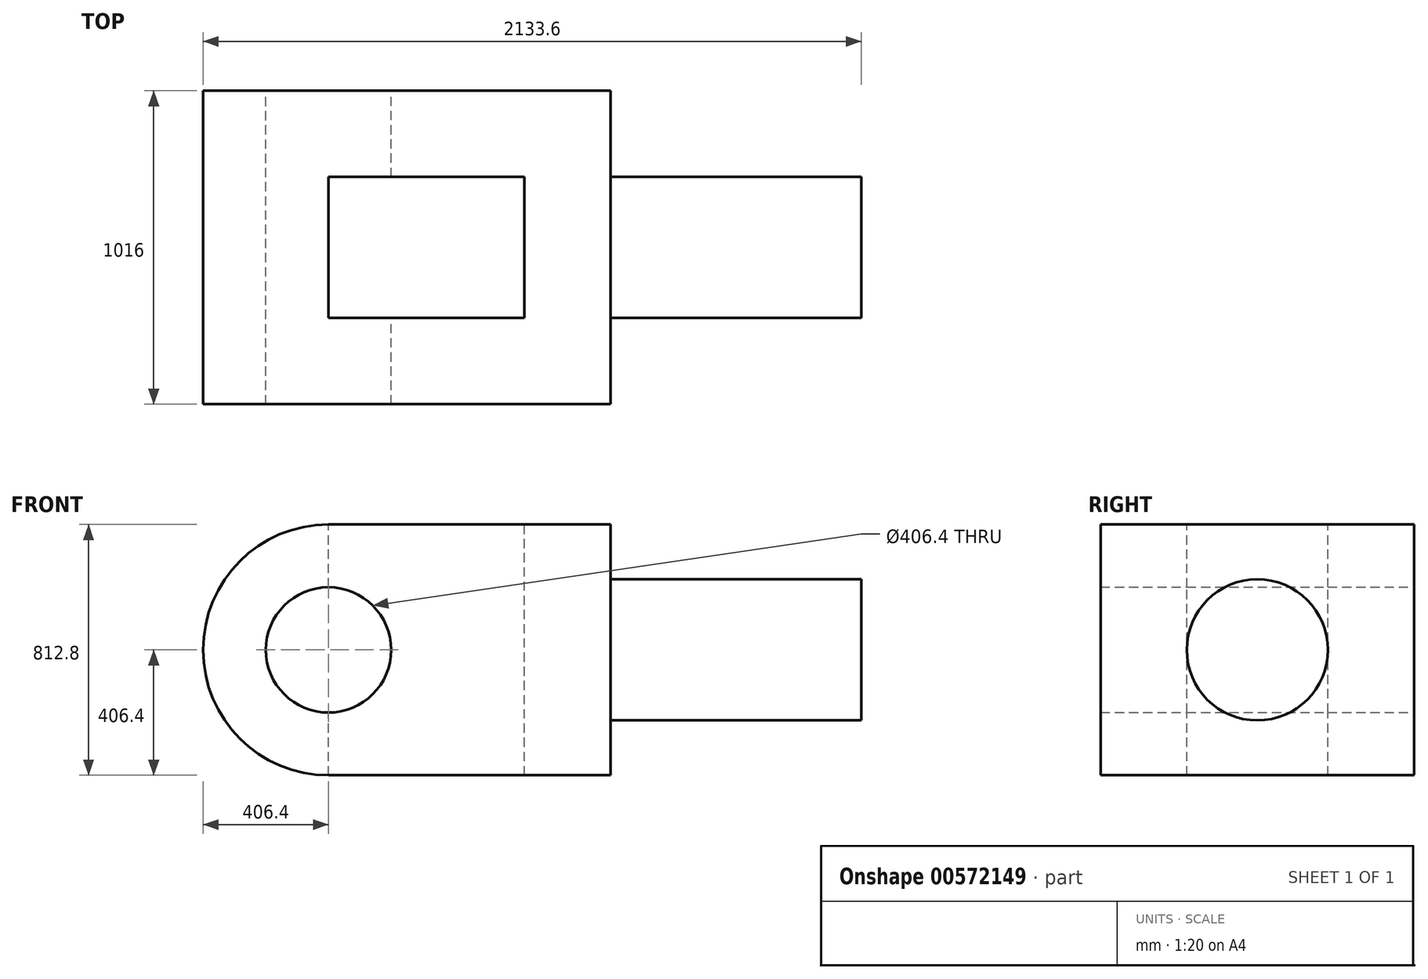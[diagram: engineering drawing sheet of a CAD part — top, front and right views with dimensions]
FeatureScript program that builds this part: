
annotation { "Feature Type Name" : "Feature", "Feature Type Description" : "" }
export const myFeature = defineFeature(function(context is Context, id is Id, definition is map)
    precondition{}
    {
        {
            var Q0;
            Q0=qCreatedBy(makeId("Front.planeOp"),FACE);
            var sketch = newSketch(context, id + "F0", { "sketchPlane" : qUnion([Q0])});
            skCircle(sketch, "E0", {"center": v(0, 0) * mm, "radius": 203.2 * mm});
            skCircle(sketch, "E1", {"center": v(0, 0) * mm, "radius": 406.4 * mm});
            skLineSegment(sketch, "E2", {"start": v(0, 406.4) * mm, "end": v(914.4, 406.4) * mm});
            skLineSegment(sketch, "E3", {"start": v(0, -406.4) * mm, "end": v(914.4, -406.4) * mm});
            skLineSegment(sketch, "E4", {"start": v(914.4, -406.4) * mm, "end": v(914.4, 406.4) * mm});
            skPoint(sketch, "E5.endSnap0", {"position": v(914.4, 0) * mm});
            skLineSegment(sketch, "E6", {"start": v(1727.2, 0) * mm, "end": v(1727.2, 228.6) * mm});
            skLineSegment(sketch, "E7", {"start": v(1727.2, 228.6) * mm, "end": v(1727.2, -228.6) * mm});
            skPoint(sketch, "E7.endSnap0", {"position": v(1727.2, 114.3) * mm});
            skLineSegment(sketch, "E8", {"start": v(1727.2, 228.6) * mm, "end": v(914.4, 228.6) * mm});
            skLineSegment(sketch, "E9", {"start": v(1727.2, -228.6) * mm, "end": v(914.4, -228.6) * mm});
            skSolve(sketch);
        }
        {
            var Q0;
            Q0=makeQuery(id+"F0.imprint","IMPRINT",FACE,{"disambiguationData":[TD([[makeQuery(id+"F0.imprint","IMPRINT",EDGE,{"derivedFrom":sQuery(id+"F0.wireOp",EDGE,"E0")}),-1.0]])]});
            var Q1;
            {var subQ3=sQuery(id+"F0.wireOp",EDGE,"E2");Q1=makeQuery(id+"F0.imprint","IMPRINT",FACE,{"disambiguationData":[TD([[makeQuery(id+"F0.imprint","IMPRINT",EDGE,{"derivedFrom":subQ3}),-1.0]])]});}
            extrude(context, id + "F1", {"entities" : qUnion([Q0, Q1]), "depth" : 508 * mm, "offsetDistance" : 25.4 * mm});
        }
        {
            var Q0;
            Q0=makeQuery(id+"F0.imprint","IMPRINT",FACE,{"disambiguationData":[TD([[makeQuery(id+"F0.imprint","IMPRINT",EDGE,{"derivedFrom":sQuery(id+"F0.wireOp",EDGE,"E0")}),-1.0]])]});
            var Q1;
            {var subQ3=sQuery(id+"F0.wireOp",EDGE,"E2");Q1=makeQuery(id+"F0.imprint","IMPRINT",FACE,{"disambiguationData":[TD([[makeQuery(id+"F0.imprint","IMPRINT",EDGE,{"derivedFrom":subQ3}),-1.0]])]});}
            extrude(context, id + "F2", {"entities" : qUnion([Q0, Q1]), "operationType" : NewBodyOperationType.ADD, "oppositeDirection" : true, "depth" : 508 * mm, "offsetDistance" : 25.4 * mm});
        }
        {
            var Q0;
            {var subQ0=sQuery(id+"F0.wireOp",EDGE,"E4");Q0=makeQuery(id+"F2.boolean.opBoolean","MERGE",FACE,{"derivedFrom":[makeQuery(id+"F1.opExtrude","SWEPT_FACE",FACE,{"disambiguationData":[OSD([subQ0])]}),makeQuery(id+"F2.opExtrude","SWEPT_FACE",FACE,{"disambiguationData":[OSD([subQ0])]})]});}
            var sketch = newSketch(context, id + "F3", { "sketchPlane" : qUnion([Q0])});
            skCircle(sketch, "E10", {"center": v(0, 0) * mm, "radius": 228.6 * mm});
            skSolve(sketch);
        }
        {
            var Q0;
            Q0 = qSketchRegion(id + "F3", true);
            extrude(context, id + "F4", {"entities" : qUnion([Q0]), "operationType" : NewBodyOperationType.ADD, "depth" : 812.8 * mm, "offsetDistance" : 25.4 * mm});
        }
        {
            var Q0;
            {var subQ0=sQuery(id+"F0.wireOp",EDGE,"E2");Q0=makeQuery(id+"F2.boolean.opBoolean","MERGE",FACE,{"derivedFrom":[makeQuery(id+"F1.opExtrude","SWEPT_FACE",FACE,{"disambiguationData":[OSD([subQ0])]}),makeQuery(id+"F2.opExtrude","SWEPT_FACE",FACE,{"disambiguationData":[OSD([subQ0])]})]});}
            var sketch = newSketch(context, id + "F5", { "sketchPlane" : qUnion([Q0])});
            skLineSegment(sketch, "E11.bottom", {"start": v(914.4, 508) * mm, "end": v(-406.4, 508) * mm});
            skLineSegment(sketch, "E11.top", {"start": v(914.4, -508) * mm, "end": v(-406.4, -508) * mm});
            skLineSegment(sketch, "E11.left", {"start": v(914.4, 508) * mm, "end": v(914.4, -508) * mm});
            skLineSegment(sketch, "E11.right", {"start": v(-406.4, 508) * mm, "end": v(-406.4, -508) * mm});
            skLineSegment(sketch, "E12", {"start": v(-406.4, 508) * mm, "end": v(-406.4, 228.6) * mm});
            skLineSegment(sketch, "E13.bottom", {"start": v(-406.4, 228.6) * mm, "end": v(635, 228.6) * mm});
            skLineSegment(sketch, "E13.top", {"start": v(-406.4, -228.6) * mm, "end": v(635, -228.6) * mm});
            skLineSegment(sketch, "E13.left", {"start": v(-406.4, 228.6) * mm, "end": v(-406.4, -228.6) * mm});
            skLineSegment(sketch, "E13.right", {"start": v(635, 228.6) * mm, "end": v(635, -228.6) * mm});
            skSolve(sketch);
        }
        {
            var Q0;
            {var subQ0=sQuery(id+"F5.wireOp",EDGE,"E13.right");Q0=makeQuery(id+"F5.imprint","IMPRINT",FACE,{"disambiguationData":[TD([[makeQuery(id+"F5.imprint","IMPRINT",EDGE,{"derivedFrom":subQ0}),-1.0]])]});}
            var Q1;
            {var subQ0=sQuery(id+"F5.wireOp",EDGE,"E13.left");Q1=makeQuery(id+"F5.imprint","IMPRINT",FACE,{"disambiguationData":[TD([[makeQuery(id+"F5.imprint","IMPRINT",EDGE,{"derivedFrom":subQ0}),1.0]])]});}
            extrude(context, id + "F6", {"entities" : qUnion([Q0, Q1]), "operationType" : NewBodyOperationType.REMOVE, "endBound" : BoundingType.THROUGH_ALL, "oppositeDirection" : true, "depth" : 25.4 * mm, "offsetDistance" : 25.4 * mm});
        }
    });
